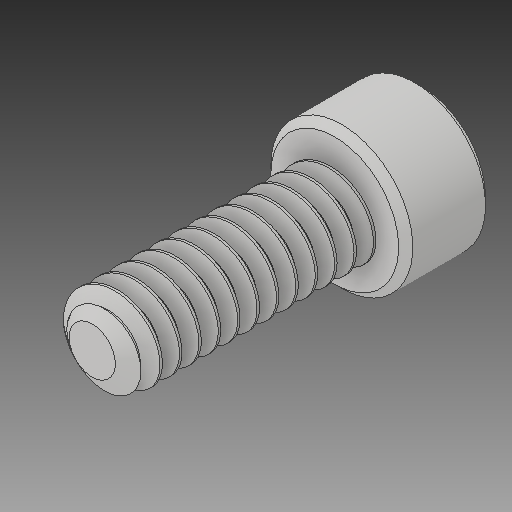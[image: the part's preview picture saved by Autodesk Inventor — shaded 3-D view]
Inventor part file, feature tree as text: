
AUTODESK INVENTOR PART (.ipt)
format: ipt  version: 2018 (Build 220112000, 112)  size: 783,360 bytes
history: native  units: in
note: dims shown in document units (in); Inventor stores cm internally (conversion verified against a paired STEP export)
features: chamfer x1
ambient origin geometry x8: Origin, YZ Plane, XZ Plane, XY Plane, X Axis, Y Axis, Z Axis, Center Point
bodies: Solid1 (feature_tree)
feature tree (1):
  chamfer  "Chamfer1"  [1 undecoded]
note: 1 required parameter value undecoded (feature->parameter linkage not recoverable at this tier; creation-order binding heuristic only, values carry confidence <= 0.55)
